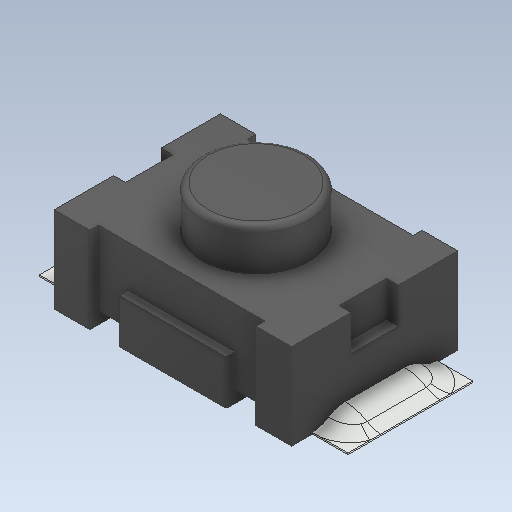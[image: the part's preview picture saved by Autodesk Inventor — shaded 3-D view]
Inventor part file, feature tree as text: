
AUTODESK INVENTOR PART (.ipt)
format: ipt  version: 2020 (Build 240168000, 168)  size: 221,696 bytes
history: native  units: in
note: dims shown in document units (in); Inventor stores cm internally (conversion verified against a paired STEP export)
features: fillet x1
ambient origin geometry x8: Origin, YZ Plane, XZ Plane, XY Plane, X Axis, Y Axis, Z Axis, Center Point
bodies: Solid1 (feature_tree)
feature tree (1):
  fillet  "Fillet3"  [1 undecoded]
note: 1 required parameter value undecoded (feature->parameter linkage not recoverable at this tier; creation-order binding heuristic only, values carry confidence <= 0.55)
